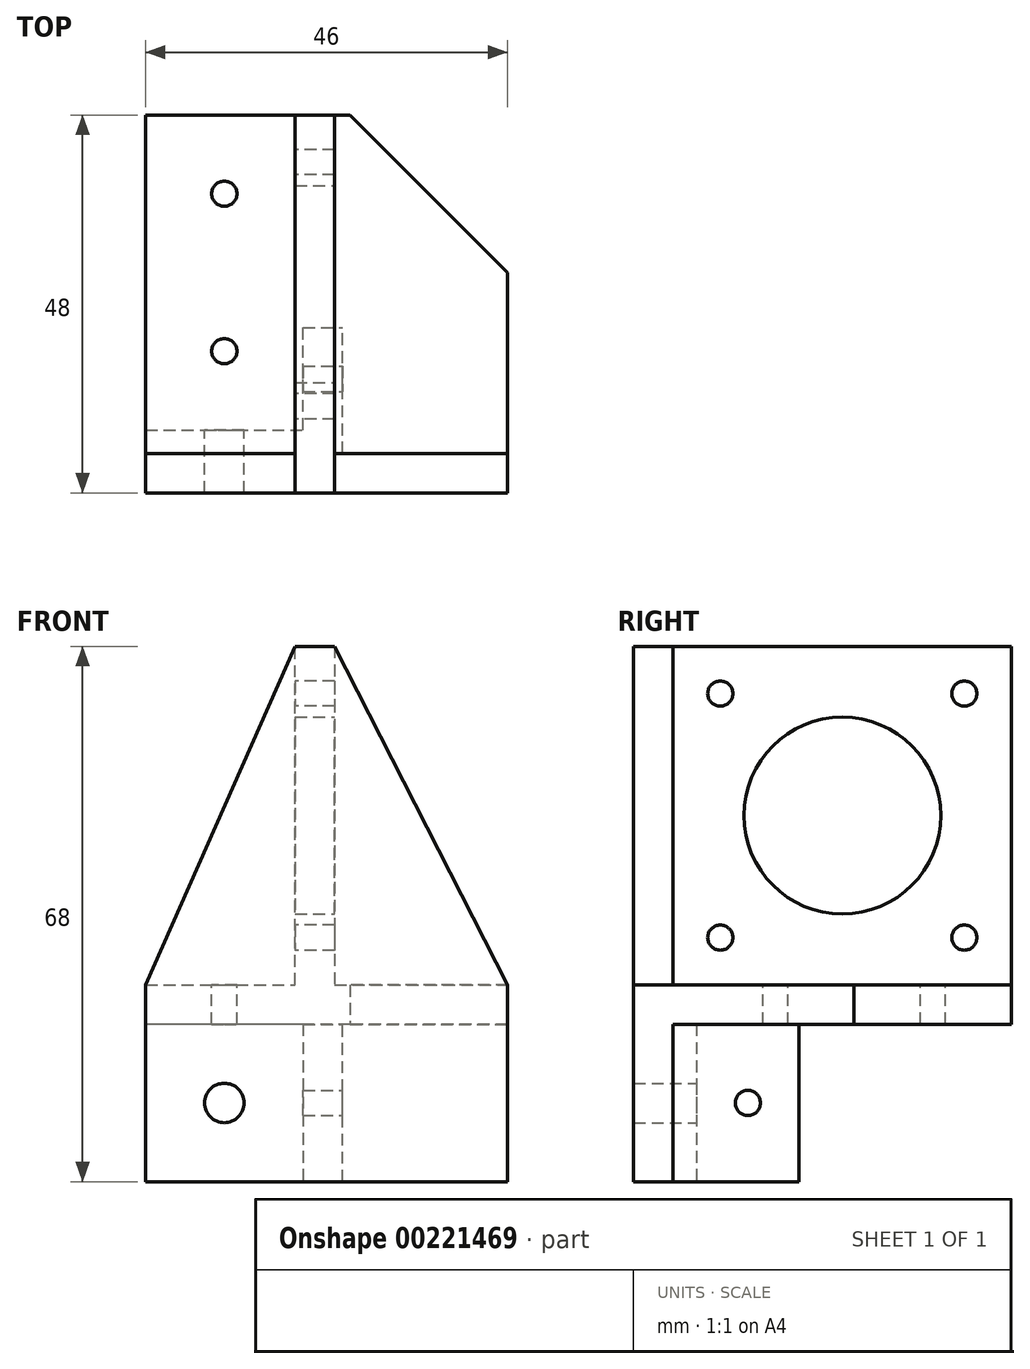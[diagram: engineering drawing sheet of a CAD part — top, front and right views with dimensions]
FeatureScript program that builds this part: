
annotation { "Feature Type Name" : "Feature", "Feature Type Description" : "" }
export const myFeature = defineFeature(function(context is Context, id is Id, definition is map)
    precondition{}
    {
        {
            var Q0;
            Q0=qCreatedBy(makeId("Front.planeOp"),FACE);
            var sketch = newSketch(context, id + "F0", { "sketchPlane" : qUnion([Q0])});
            skLineSegment(sketch, "E0.bottom", {"start": v(0, 20) * mm, "end": v(20, 20) * mm, "construction": true});
            skLineSegment(sketch, "E0.top", {"start": v(0, 0) * mm, "end": v(20, 0) * mm, "construction": true});
            skLineSegment(sketch, "E0.left", {"start": v(0, 20) * mm, "end": v(0, 0) * mm, "construction": true});
            skLineSegment(sketch, "E0.right", {"start": v(20, 20) * mm, "end": v(20, 0) * mm, "construction": true});
            skLineSegment(sketch, "E1", {"start": v(0, 20) * mm, "end": v(0, 25) * mm});
            skLineSegment(sketch, "E2", {"start": v(46, 25) * mm, "end": v(46, 20) * mm});
            skLineSegment(sketch, "E3", {"start": v(46, 20) * mm, "end": v(25, 20) * mm});
            skLineSegment(sketch, "E4", {"start": v(25, 20) * mm, "end": v(25, 0) * mm});
            skLineSegment(sketch, "E5", {"start": v(25, 0) * mm, "end": v(20, 0) * mm});
            skLineSegment(sketch, "E6", {"start": v(20, 20) * mm, "end": v(0, 20) * mm});
            skLineSegment(sketch, "E7", {"start": v(20, 20) * mm, "end": v(20, 0) * mm});
            skLineSegment(sketch, "E8", {"start": v(0, 25) * mm, "end": v(19, 25) * mm});
            skLineSegment(sketch, "E9", {"start": v(19, 25) * mm, "end": v(19, 68) * mm});
            skLineSegment(sketch, "E10", {"start": v(19, 68) * mm, "end": v(24, 68) * mm});
            skLineSegment(sketch, "E11", {"start": v(24, 68) * mm, "end": v(24, 25) * mm});
            skLineSegment(sketch, "E12", {"start": v(24, 25) * mm, "end": v(46, 25) * mm});
            skSolve(sketch);
        }
        {
            var Q0;
            Q0=makeQuery(id+"F0.imprint","IMPRINT",FACE,{"disambiguationData":[TD([[makeQuery(id+"F0.imprint","IMPRINT",EDGE,{"derivedFrom":sQuery(id+"F0.wireOp",EDGE,"E1")}),-1.0]])]});
            extrude(context, id + "F1", {"entities" : qUnion([Q0]), "depth" : 43 * mm});
        }
        {
            var Q0;
            Q0=makeQuery(id+"F1.opExtrude","CAP_FACE",FACE,{"disambiguationData":[OSD([sQuery(id+"F0.wireOp",EDGE,"E1"),sQuery(id+"F0.wireOp",EDGE,"E2"),sQuery(id+"F0.wireOp",EDGE,"E3"),sQuery(id+"F0.wireOp",EDGE,"E4"),sQuery(id+"F0.wireOp",EDGE,"E5"),sQuery(id+"F0.wireOp",EDGE,"E6"),sQuery(id+"F0.wireOp",EDGE,"E7"),sQuery(id+"F0.wireOp",EDGE,"E8"),sQuery(id+"F0.wireOp",EDGE,"E9"),sQuery(id+"F0.wireOp",EDGE,"E10"),sQuery(id+"F0.wireOp",EDGE,"E11"),sQuery(id+"F0.wireOp",EDGE,"E12")])],"isStart":false});
            var sketch = newSketch(context, id + "F2", { "sketchPlane" : qUnion([Q0])});
            skLineSegment(sketch, "E13.bottom", {"start": v(0, 20) * mm, "end": v(20, 20) * mm});
            skLineSegment(sketch, "E13.top", {"start": v(0, 0) * mm, "end": v(20, 0) * mm});
            skLineSegment(sketch, "E13.left", {"start": v(0, 20) * mm, "end": v(0, 0) * mm});
            skLineSegment(sketch, "E13.right", {"start": v(20, 20) * mm, "end": v(20, 0) * mm});
            skSolve(sketch);
        }
        {
            var Q0;
            Q0 = qSketchRegion(id + "F2", true);
            extrude(context, id + "F3", {"entities" : qUnion([Q0]), "operationType" : NewBodyOperationType.ADD, "oppositeDirection" : true, "depth" : 3 * mm});
        }
        {
            var Q0;
            Q0=makeQuery(id+"F1.opExtrude","SWEPT_FACE",FACE,{"disambiguationData":[OSD([sQuery(id+"F0.wireOp",EDGE,"E4")])]});
            var sketch = newSketch(context, id + "F4", { "sketchPlane" : qUnion([Q0])});
            skLineSegment(sketch, "E14.bottom", {"start": v(0, 0) * mm, "end": v(-27, 0) * mm});
            skLineSegment(sketch, "E14.top", {"start": v(0, 20) * mm, "end": v(-27, 20) * mm});
            skLineSegment(sketch, "E14.left", {"start": v(0, 0) * mm, "end": v(0, 20) * mm});
            skLineSegment(sketch, "E14.right", {"start": v(-27, 0) * mm, "end": v(-27, 20) * mm});
            skSolve(sketch);
        }
        {
            var Q0;
            Q0=makeQuery(id+"F4.imprint","IMPRINT",FACE,{"disambiguationData":[TD([[makeQuery(id+"F4.imprint","IMPRINT",EDGE,{"derivedFrom":sQuery(id+"F4.wireOp",EDGE,"E14.bottom")}),1.0]])]});
            var Q1;
            Q1=makeQuery(id+"F1.opExtrude","SWEPT_FACE",FACE,{"disambiguationData":[OSD([sQuery(id+"F0.wireOp",EDGE,"E7")])]});
            extrude(context, id + "F5", {"entities" : qUnion([Q0]), "operationType" : NewBodyOperationType.REMOVE, "endBound" : BoundingType.UP_TO_SURFACE, "oppositeDirection" : true, "endBoundEntityFace" : qUnion([Q1]), "depth" : 25 * mm});
        }
        {
            var Q0;
            Q0=makeQuery(id+"F1.opExtrude","SWEPT_FACE",FACE,{"disambiguationData":[OSD([sQuery(id+"F0.wireOp",EDGE,"E11")])]});
            var sketch = newSketch(context, id + "F6", { "sketchPlane" : qUnion([Q0])});
            skLineSegment(sketch, "E15", {"start": v(-43, 68) * mm, "end": v(0, 25) * mm, "construction": true});
            skLineSegment(sketch, "E16", {"start": v(0, 68) * mm, "end": v(-43, 25) * mm, "construction": true});
            skPoint(sketch, "E17", {"position": v(-37, 62) * mm});
            skPoint(sketch, "E18", {"position": v(-6, 62) * mm});
            skPoint(sketch, "E19", {"position": v(-6, 31) * mm});
            skPoint(sketch, "E20", {"position": v(-37, 31) * mm});
            skSolve(sketch);
        }
        {
            var Q0;
            Q0=makeQuery(id+"F1.opExtrude","SWEPT_FACE",FACE,{"disambiguationData":[OSD([sQuery(id+"F0.wireOp",EDGE,"E11")])]});
            var sketch = newSketch(context, id + "F7", { "sketchPlane" : qUnion([Q0])});
            skCircle(sketch, "E21", {"center": v(-21.5, 46.5) * mm, "radius": 12.5 * mm});
            skPoint(sketch, "E21.centerSnap0", {"position": v(-43, 46.5) * mm});
            skPoint(sketch, "E21.centerSnap1", {"position": v(-21.5, 68) * mm});
            skSolve(sketch);
        }
        {
            var Q0;
            Q0=makeQuery(id+"F7.imprint","IMPRINT",FACE,{"disambiguationData":[TD([[makeQuery(id+"F7.imprint","IMPRINT",EDGE,{"derivedFrom":sQuery(id+"F7.wireOp",EDGE,"E21")}),1.0]])]});
            var Q1;
            Q1=makeQuery(id+"F1.opExtrude","SWEPT_FACE",FACE,{"disambiguationData":[OSD([sQuery(id+"F0.wireOp",EDGE,"E9")])]});
            extrude(context, id + "F8", {"entities" : qUnion([Q0]), "operationType" : NewBodyOperationType.REMOVE, "endBound" : BoundingType.UP_TO_SURFACE, "oppositeDirection" : true, "endBoundEntityFace" : qUnion([Q1]), "depth" : 25 * mm});
        }
        {
            var Q0;
            Q0=makeQuery(id+"F5.boolean.opBoolean","MERGE",FACE,{"derivedFrom":[makeQuery(id+"F1.opExtrude","SWEPT_FACE",FACE,{"disambiguationData":[OSD([sQuery(id+"F0.wireOp",EDGE,"E3")])]}),makeQuery(id+"F1.opExtrude","SWEPT_FACE",FACE,{"disambiguationData":[OSD([sQuery(id+"F0.wireOp",EDGE,"E6")])]}),makeQuery(id+"F5.opExtrude","SWEPT_FACE",FACE,{"disambiguationData":[OSD([sQuery(id+"F4.wireOp",EDGE,"E14.top")])]})]});
            var sketch = newSketch(context, id + "F9", { "sketchPlane" : qUnion([Q0])});
            skPoint(sketch, "E22", {"position": v(10, 30) * mm});
            skPoint(sketch, "E22.positionSnap0", {"position": v(10, 40) * mm});
            skPoint(sketch, "E23", {"position": v(10, 10) * mm});
            skSolve(sketch);
        }
        {
            var Q0;
            Q0=makeQuery(id+"F1.opExtrude","SWEPT_FACE",FACE,{"disambiguationData":[OSD([sQuery(id+"F0.wireOp",EDGE,"E7")])]});
            var sketch = newSketch(context, id + "F10", { "sketchPlane" : qUnion([Q0])});
            skPoint(sketch, "E24", {"position": v(33.5, 10) * mm});
            skPoint(sketch, "E24.positionSnap0", {"position": v(33.5, 0) * mm});
            skPoint(sketch, "E24.positionSnap1", {"position": v(27, 10) * mm});
            skSolve(sketch);
        }
        {
            var Q0;
            Q0=sQuery(id+"F6.wireOp",VERTEX,"E17");
            var Q1;
            Q1=sQuery(id+"F6.wireOp",VERTEX,"E18");
            var Q2;
            Q2=sQuery(id+"F6.wireOp",VERTEX,"E20");
            var Q3;
            Q3=sQuery(id+"F6.wireOp",VERTEX,"E19");
            var Q4;
            Q4=sQuery(id+"F9.wireOp",VERTEX,"E23");
            var Q5;
            Q5=sQuery(id+"F9.wireOp",VERTEX,"E22");
            var Q6;
            Q6=sQuery(id+"F10.wireOp",VERTEX,"E24");
            var Q7;
            Q7=makeQuery(id+"F1.opExtrude","SWEPT_BODY",BODY,{"disambiguationData":[OSD([sQuery(id+"F0.wireOp",EDGE,"E1"),sQuery(id+"F0.wireOp",EDGE,"E2"),sQuery(id+"F0.wireOp",EDGE,"E3"),sQuery(id+"F0.wireOp",EDGE,"E4"),sQuery(id+"F0.wireOp",EDGE,"E5"),sQuery(id+"F0.wireOp",EDGE,"E6"),sQuery(id+"F0.wireOp",EDGE,"E7"),sQuery(id+"F0.wireOp",EDGE,"E8"),sQuery(id+"F0.wireOp",EDGE,"E9"),sQuery(id+"F0.wireOp",EDGE,"E10"),sQuery(id+"F0.wireOp",EDGE,"E11"),sQuery(id+"F0.wireOp",EDGE,"E12")])]});
            hole(context, id + "F11", {"style" : HoleStyle.SIMPLE, "endStyle" : HoleEndStyle.THROUGH, "standardTappedOrClearance" : lookupTablePath({ "standard" : "ISO", "size" : "3.2", "type" : "Drilled" }), "standardBlindInLast" : lookupTablePath({ "standard" : "ISO", "size" : "3.2", "type" : "Drilled" }), "holeDiameter" : 3.2 * mm, "locations" : qUnion([Q0, Q1, Q2, Q3, Q4, Q5, Q6]), "scope" : qUnion([Q7]), "isTappedThrough" : true});
        }
        {
            var Q0;
            Q0=makeQuery(id+"F3.boolean.opBoolean","MERGE",FACE,{"derivedFrom":[makeQuery(id+"F1.opExtrude","CAP_FACE",FACE,{"disambiguationData":[OSD([sQuery(id+"F0.wireOp",EDGE,"E1"),sQuery(id+"F0.wireOp",EDGE,"E2"),sQuery(id+"F0.wireOp",EDGE,"E3"),sQuery(id+"F0.wireOp",EDGE,"E4"),sQuery(id+"F0.wireOp",EDGE,"E5"),sQuery(id+"F0.wireOp",EDGE,"E6"),sQuery(id+"F0.wireOp",EDGE,"E7"),sQuery(id+"F0.wireOp",EDGE,"E8"),sQuery(id+"F0.wireOp",EDGE,"E9"),sQuery(id+"F0.wireOp",EDGE,"E10"),sQuery(id+"F0.wireOp",EDGE,"E11"),sQuery(id+"F0.wireOp",EDGE,"E12")])],"isStart":false}),makeQuery(id+"F3.opExtrude","CAP_FACE",FACE,{"disambiguationData":[OSD([sQuery(id+"F2.wireOp",EDGE,"E13.bottom"),sQuery(id+"F2.wireOp",EDGE,"E13.top"),sQuery(id+"F2.wireOp",EDGE,"E13.left"),sQuery(id+"F2.wireOp",EDGE,"E13.right")])],"isStart":true})]});
            var sketch = newSketch(context, id + "F12", { "sketchPlane" : qUnion([Q0])});
            skLineSegment(sketch, "E25", {"start": v(0, 25) * mm, "end": v(19, 68) * mm});
            skLineSegment(sketch, "E26", {"start": v(19, 68) * mm, "end": v(24, 68) * mm});
            skLineSegment(sketch, "E27", {"start": v(24, 68) * mm, "end": v(46, 25) * mm});
            skLineSegment(sketch, "E28", {"start": v(46, 25) * mm, "end": v(46, 20) * mm});
            skLineSegment(sketch, "E29", {"start": v(0, 0) * mm, "end": v(0, 25) * mm});
            skLineSegment(sketch, "E30", {"start": v(0, 0) * mm, "end": v(46, 0) * mm});
            skLineSegment(sketch, "E31", {"start": v(46, 0) * mm, "end": v(46, 20) * mm});
            skSolve(sketch);
        }
        {
            var Q0;
            Q0=makeQuery(id+"F12.imprint","IMPRINT",FACE,{"disambiguationData":[TD([[makeQuery(id+"F12.imprint","IMPRINT",EDGE,{"derivedFrom":sQuery(id+"F12.wireOp",EDGE,"E25")}),-1.0]])]});
            var Q1;
            Q1=makeQuery(id+"F12.imprint","IMPRINT",FACE,{"disambiguationData":[TD([[makeQuery(id+"F12.imprint","IMPRINT",EDGE,{"derivedFrom":sQuery(id+"F12.wireOp",EDGE,"E26")}),-1.0]])]});
            var Q2;
            Q2=makeQuery(id+"F12.imprint","IMPRINT",FACE,{"disambiguationData":[TD([[makeQuery(id+"F12.imprint","IMPRINT",EDGE,{"derivedFrom":sQuery(id+"F12.wireOp",EDGE,"E27")}),-1.0]])]});
            var Q3;
            {var subQ2=sQuery(id+"F12.wireOp",EDGE,"E31");Q3=makeQuery(id+"F12.imprint","IMPRINT",FACE,{"disambiguationData":[TD([[makeQuery(id+"F12.imprint","IMPRINT",EDGE,{"derivedFrom":subQ2}),1.0]])]});}
            extrude(context, id + "F13", {"entities" : qUnion([Q0, Q1, Q2, Q3]), "operationType" : NewBodyOperationType.ADD, "depth" : 5 * mm});
        }
        {
            var Q0;
            Q0=makeQuery(id+"F1.opExtrude","CAP_EDGE",EDGE,{"disambiguationData":[OSD([sQuery(id+"F0.wireOp",EDGE,"E2")])],"isStart":true});
            chamfer(context, id + "F14", {"entities" : qUnion([Q0]), "width" : 20 * mm, "tangentPropagation" : true});
        }
        {
            var Q0;
            Q0=makeQuery(id+"F3.opExtrude","CAP_FACE",FACE,{"disambiguationData":[OSD([sQuery(id+"F2.wireOp",EDGE,"E13.bottom"),sQuery(id+"F2.wireOp",EDGE,"E13.top"),sQuery(id+"F2.wireOp",EDGE,"E13.left"),sQuery(id+"F2.wireOp",EDGE,"E13.right")])],"isStart":false});
            var sketch = newSketch(context, id + "F15", { "sketchPlane" : qUnion([Q0])});
            skPoint(sketch, "E32", {"position": v(-10, 0) * mm});
            skPoint(sketch, "E33", {"position": v(0, 10) * mm});
            skCircle(sketch, "E34", {"center": v(-10, 10) * mm, "radius": 2.5 * mm});
            skSolve(sketch);
        }
        {
            var Q0;
            Q0=makeQuery(id+"F15.imprint","IMPRINT",FACE,{"disambiguationData":[TD([[makeQuery(id+"F15.imprint","IMPRINT",EDGE,{"derivedFrom":sQuery(id+"F15.wireOp",EDGE,"E34")}),1.0]])]});
            var Q1;
            Q1=makeQuery(id+"F13.opExtrude","CAP_FACE",FACE,{"disambiguationData":[OSD([sQuery(id+"F12.wireOp",EDGE,"E25"),sQuery(id+"F12.wireOp",EDGE,"E26"),sQuery(id+"F12.wireOp",EDGE,"E27"),sQuery(id+"F12.wireOp",EDGE,"E28"),sQuery(id+"F12.wireOp",EDGE,"E29"),sQuery(id+"F12.wireOp",EDGE,"E30"),sQuery(id+"F12.wireOp",EDGE,"E31")])],"isStart":false});
            extrude(context, id + "F16", {"entities" : qUnion([Q0]), "operationType" : NewBodyOperationType.REMOVE, "endBound" : BoundingType.UP_TO_SURFACE, "oppositeDirection" : true, "endBoundEntityFace" : qUnion([Q1]), "depth" : 25 * mm});
        }
    });
